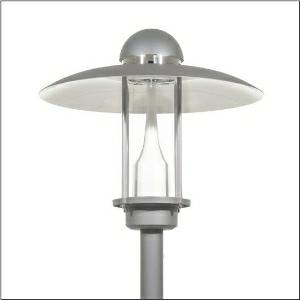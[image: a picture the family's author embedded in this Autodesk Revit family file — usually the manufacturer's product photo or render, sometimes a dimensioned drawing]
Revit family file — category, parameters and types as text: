
# Revit family: city-light_elegance_iq___st1_2a_5xa5265kf14h_1fe5
name_source: partatom
category: Lighting Fixtures
units: mm (PartAtom-declared; Revit-internal decimal feet)

## family parameters
Cut with Voids When Loaded = No
Host = Face
Light Source = No
Part Type = Normal
Room Calculation Point = No
Round Connector Dimension = Use Diameter
Shared = No

## types (1)
- --- (1 x LED, 1470 lm, 10 W, 4000K)
    Apparent Load = 10 VA
    CIE Flux Codes = 22 62 94 98 100
    Color Rendering = 70
    Color Temperature = 4000K
    Default Elevation = 1800 mm
    Description = City-Light Elegance iQ, mast luminaire, Module 540 iQ-SR, primary light control with 3 zone facetted reflector, of plastic, silver coated, highly specular, structured, primary optical cover: cover, of PMMA, transparent, light distribution: ST1.2a, light emission: direct distribution, primary light characteristic: asymmetric, installation type: post-top, LED, High Power LED, rated luminous flux: 1.470lm, luminous efficacy: 147lm/W, light colour: 740, colour temperature: 4000K, control gear: ECG iQ, control: presetting dimming logarithmic, Street-Remote, Auto-Match, Temp-Guard, Lumen-Switch, Night-Set, Smart-Wire, Light-Fading, Desk-Remote (wireless, voltage-free reading and setting of iQ features in the workshop via application-optimized NFC function/RFID function), optimised constant luminous flux control (CLO 2.0), with terminal, 6-pole, max. 2.5mm², mains connection: 220..240V, AC, 50/60Hz, start of lifetime: 10W, end of lifetime: 10W, reduction: 5W, luminaire housing, upper part, of aluminium, coated, Siteco® metallic grey (DB 702S), diameter: 750mm, height: 675mm, spigot size: d x l = 76 x 70mm (post-top) | with reducer (optional accessory) 60 x 70mm, post-top mast mounting element, of diecast aluminium, coated, Siteco® metallic grey (DB 702S), Module 540 iQ-SR, traffic white (RAL 9016), equipment: standard, protection rating (complete): IP65, insulation class (complete): insulation class II (safety insulation), certification: CE, ENEC, VDE, packaging unit: 1 piece

Light Distribution: ST1.2a
    Height = 675 mm
    Lamp = 1 x LED
    Lamp Light Flux = 1470 lm
    Lamp Power = 10 W
    Lamp count = 1
    Length = 750 mm
    Luminous efficacy = 147 lm/W
    Manufacturer = Siteco
    ModVariant = No
    Model = 5XA5265KF14H
    Number of Poles = 1
    OnlyDefault = Yes
    Power Factor = 1
    Product Name = City-Light Elegance iQ | ST1.2a
    Product group = mast luminaire | pylon top
    ProductGroupID = 6100
    Protection Class = Protection class II
    Protection Degree = IP 65
    RLX_Detail_Level = 1
    RlxData = <blob elided: 103909 chars, md5=e3123560>
    Socket = socket
    Standby Power = 0 W
    System Light Flux = 1470 lm
    System Power = 10 W
    Type Comments = factory setting: luminous flux: 100 % | dim-lin: 254 | 401 mA
    Type Image = l_1006912.jpg
    URL = http://relux.com
    VarID = @adj_071069
    Voltage = 0 V
    Weight = 0.00 kg
    Width = 0 mm  [stored 0 ft]

note: [stored X ft] marks values corroborated as IEEE doubles in the binary element streams (Revit-internal decimal feet)

## geometry (parser evidence)
native form markers: Blend x4, Sweep x12
no freeform markers — native parametric forms only
